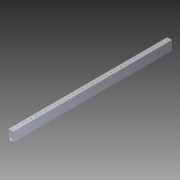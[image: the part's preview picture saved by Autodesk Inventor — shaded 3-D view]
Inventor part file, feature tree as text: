
AUTODESK INVENTOR PART (.ipt)
format: ipt  version: 2014 SP1 (Build 180222100, 222)  size: 753,152 bytes
history: native  units: in
note: dims shown in document units (in); Inventor stores cm internally (conversion verified against a paired STEP export)
features: other x2, extrude x1, imported_body x1, sketch x1
ambient origin geometry x8: Origin, YZ Plane, XZ Plane, XY Plane, X Axis, Y Axis, Z Axis, Center Point
bodies: Body1 (feature_tree)
feature tree (5):
  other  "Cut-Extrude2"
  other  "2x1 Tube1"
  extrude  "Extrusion1"  [1 undecoded]
  imported_body  "Base1"
  sketch  "Sketch1"  dims[d0=23.0in d1=0.0in]
note: 1 required parameter value undecoded (feature->parameter linkage not recoverable at this tier; creation-order binding heuristic only, values carry confidence <= 0.55)
